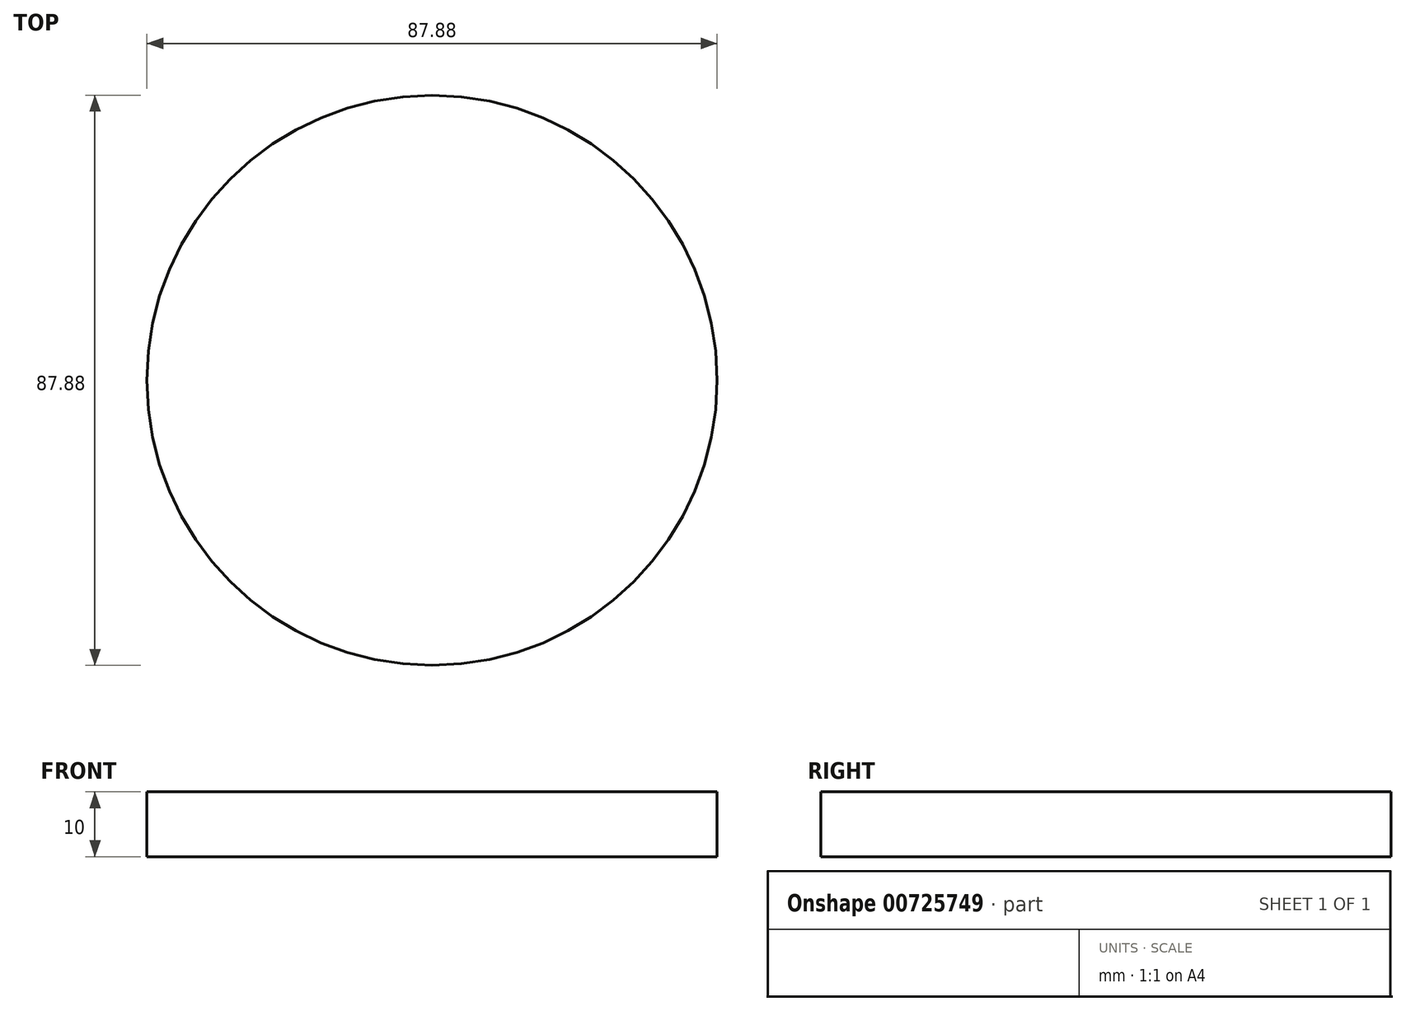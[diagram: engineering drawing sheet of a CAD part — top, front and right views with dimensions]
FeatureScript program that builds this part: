
annotation { "Feature Type Name" : "Feature", "Feature Type Description" : "" }
export const myFeature = defineFeature(function(context is Context, id is Id, definition is map)
    precondition{}
    {
        {
            var Q0;
            Q0=qCreatedBy(makeId("Top.planeOp"),FACE);
            var sketch = newSketch(context, id + "F0", { "sketchPlane" : qUnion([Q0])});
            skCircle(sketch, "E0", {"center": v(0, 0) * mm, "radius": 43.94 * mm});
            skSolve(sketch);
        }
        {
            var Q0;
            Q0 = qSketchRegion(id + "F0", true);
            extrude(context, id + "F1", {"entities" : qUnion([Q0]), "depth" : 10 * mm, "offsetDistance" : 25 * mm});
        }
    });
